# Revit family: 柔性防水套管（A型）
name_source: partatom
category: 管道附件
revit_build: Autodesk Revit 2016 (Build: 20150220_1215(x64)
units: mm (PartAtom-declared; Revit-internal decimal feet)

## family parameters
主体 = 面
共享 = 否
加载时剪切的空心 = 否
圆形连接件大小 = 使用直径
零件类型 = 标准

## types (18) — shared parameters
l5 = 40  [stored 0.131234 ft]
默认高程 = 1219
zero-valued in all types: 高度

## per-type parameters (varying)
| type | D2_2 | D3_2 | D4 | D5 | DN | URL | b | b1 | d2 | d3 | l | l0 | l1 | l2 | n | r | δ2 | δ3 | 螺丝半径 | 角度 | 说明 |
| DN50 | 95 | 65  [stored 0.213255 ft] | 145 | 200 | 50 | www.goujianwu.com | 14  [stored 0.0459318 ft] | 12  [stored 0.0393701 ft] | 91 | 73  [stored 0.239501 ft] | 65  [stored 0.213255 ft] | 28  [stored 0.0918635 ft] | 72 | 30  [stored 0.0984252 ft] | 4 | 73  [stored 0.239501 ft] | 4  [stored 0.0131234 ft] | 8  [stored 0.0262467 ft] | 6  [stored 0.019685 ft] | 90.00° | 找构件就上构件坞 |
| DN65 | 114 | 80 | 165 | 220 | 65  [stored 0.213255 ft] | www.goujianwu.com | 14  [stored 0.0459318 ft] | 12  [stored 0.0393701 ft] | 110  [stored 0.360892 ft] | 88 | 65  [stored 0.213255 ft] | 28  [stored 0.0918635 ft] | 72 | 30  [stored 0.0984252 ft] | 4 | 83 | 4  [stored 0.0131234 ft] | 8  [stored 0.0262467 ft] | 6  [stored 0.019685 ft] | 90.00° | 找构件就上构件坞 |
| DN80 | 127 | 95 | 180 | 235 | 80 | www.goujianwu.com | 18  [stored 0.0590551 ft] | 12  [stored 0.0393701 ft] | 123 | 105 | 65  [stored 0.213255 ft] | 28  [stored 0.0918635 ft] | 76 | 38 | 4 | 90  [stored 0.295276 ft] | 4  [stored 0.0131234 ft] | 10  [stored 0.0328084 ft] | 8  [stored 0.0262467 ft] | 90.00° | 找构件就上构件坞 |
| DN100 | 146 | 114 | 200 | 255 | 100  [stored 0.328084 ft] | www.goujianwu.com | 18  [stored 0.0590551 ft] | 12  [stored 0.0393701 ft] | 142 | 124 | 65  [stored 0.213255 ft] | 28  [stored 0.0918635 ft] | 76 | 38 | 4 | 100  [stored 0.328084 ft] | 5  [stored 0.0164042 ft] | 10  [stored 0.0328084 ft] | 8  [stored 0.0262467 ft] | 90.00° | 找构件就上构件坞 |
| DN125 | 180 | 140 | 235 | 290 | 125 | www.goujianwu.com | 18  [stored 0.0590551 ft] | 12  [stored 0.0393701 ft] | 174 | 150 | 65  [stored 0.213255 ft] | 28  [stored 0.0918635 ft] | 76 | 38 | 6 | 118 | 6  [stored 0.019685 ft] | 10  [stored 0.0328084 ft] | 8  [stored 0.0262467 ft] | 60.00° | 找构件就上构件坞 |
| DN150 | 203 | 165 | 260 | 315 | 150 | www.goujianwu.com | 18  [stored 0.0590551 ft] | 12  [stored 0.0393701 ft] | 197 | 175 | 65  [stored 0.213255 ft] | 28  [stored 0.0918635 ft] | 76 | 38 | 6 | 130 | 6  [stored 0.019685 ft] | 10  [stored 0.0328084 ft] | 8  [stored 0.0262467 ft] | 60.00° | 找构件就上构件坞 |
| DN200 | 265 | 226 | 320 | 375 | 200 | www.goujianwu.com | 18  [stored 0.0590551 ft] | 12  [stored 0.0393701 ft] | 259 | 236 | 65  [stored 0.213255 ft] | 28  [stored 0.0918635 ft] | 76 | 38 | 6 | 160 | 6  [stored 0.019685 ft] | 10  [stored 0.0328084 ft] | 8  [stored 0.0262467 ft] | 60.00° | 找构件就上构件坞 |
| DN250 | 325 | 280 | 380 | 435 | 250 | www.goujianwu.com | 18  [stored 0.0590551 ft] | 12  [stored 0.0393701 ft] | 319 | 290 | 65  [stored 0.213255 ft] | 28  [stored 0.0918635 ft] | 76 | 38 | 8 | 190 | 6  [stored 0.019685 ft] | 10  [stored 0.0328084 ft] | 8  [stored 0.0262467 ft] | 45.00° | 找构件就上构件坞 |
| DN300 | 377 | 333 | 435 | 495 | 300 | www.goujianwu.com | 22  [stored 0.0721785 ft] | 16  [stored 0.0524934 ft] | 369 | 343 | 72 | 32 | 90  [stored 0.295276 ft] | 46 | 8 | 218 | 8  [stored 0.0262467 ft] | 10  [stored 0.0328084 ft] | 10  [stored 0.0328084 ft] | 45.00° | 找构件就上构件坞 |
| DN350 | 426 | 385 | 485 | 545 | 350 | www.goujianwu.com | 22  [stored 0.0721785 ft] | 16  [stored 0.0524934 ft] | 416 | 395 | 72 | 32 | 90  [stored 0.295276 ft] | 46 | 8 | 243 | 10  [stored 0.0328084 ft] | 10  [stored 0.0328084 ft] | 10  [stored 0.0328084 ft] | 45.00° | 找构件就上构件坞 |
| DN400 | 480 | 435 | 540 | 600 | 400 | www.goujianwu.com | 22  [stored 0.0721785 ft] | 16  [stored 0.0524934 ft] | 470 | 445 | 72 | 32 | 90  [stored 0.295276 ft] | 46 | 12 | 270 | 10  [stored 0.0328084 ft] | 10  [stored 0.0328084 ft] | 10  [stored 0.0328084 ft] | 30.00° | 找构件就上构件坞 |
| DN450 | 530 | 488 | 590 | 650 | 450 | www.goujianwu.com | 22  [stored 0.0721785 ft] | 16  [stored 0.0524934 ft] | 520 | 498 | 72 | 32 | 90  [stored 0.295276 ft] | 46 | 12 | 295 | 10  [stored 0.0328084 ft] | 10  [stored 0.0328084 ft] | 10  [stored 0.0328084 ft] | 30.00° | 找构件就上构件坞 |
| DN500 | 585 | 538 | 645 | 705 | 500 | www.goujianwu.com | 22  [stored 0.0721785 ft] | 16  [stored 0.0524934 ft] | 575 | 548 | 72 | 32 | 90  [stored 0.295276 ft] | 46 | 20 | 323 | 10  [stored 0.0328084 ft] | 10  [stored 0.0328084 ft] | 10  [stored 0.0328084 ft] | 18.00° | 找构件就上构件坞 |
| DN600 | 690 | 640 | 755 | 820 | 600 | www.goujianwu.com | 26 | 20  [stored 0.0656168 ft] | 680 | 652 | 75  [stored 0.246063 ft] | 40  [stored 0.131234 ft] | 104 | 54  [stored 0.177165 ft] | 20 | 378 | 10  [stored 0.0328084 ft] | 12  [stored 0.0393701 ft] | 12  [stored 0.0393701 ft] | 18.00° | 找构件就上构件坞 |
| DN700 | 780 | 730 | 845 | 910 | 700 |  | 26 | 20  [stored 0.0656168 ft] | 770 | 742 | 75  [stored 0.246063 ft] | 40  [stored 0.131234 ft] | 104 | 54  [stored 0.177165 ft] | 20 | 423 | 10  [stored 0.0328084 ft] | 12  [stored 0.0393701 ft] | 12  [stored 0.0393701 ft] | 18.00° |  |
| DN800 | 880 | 830 | 950 | 1020 | 800 | www.goujianwu.com | 30  [stored 0.0984252 ft] | 20  [stored 0.0656168 ft] | 870 | 842 | 80 | 40  [stored 0.131234 ft] | 117 | 60 | 20 | 475 | 10  [stored 0.0328084 ft] | 12  [stored 0.0393701 ft] | 27  [stored 0.0885827 ft] | 18.00° | 找构件就上构件坞 |
| DN900 | 980 | 930 | 1050 | 1120 | 900 | www.goujianwu.com | 30  [stored 0.0984252 ft] | 20  [stored 0.0656168 ft] | 970 | 942 | 80 | 40  [stored 0.131234 ft] | 117 | 60 | 20 | 525 | 10  [stored 0.0328084 ft] | 12  [stored 0.0393701 ft] | 27  [stored 0.0885827 ft] | 18.00° | 找构件就上构件坞 |
| DN1000 | 1080 | 1030 | 1150 | 1220 | 1000 | www.goujianwu.com | 30  [stored 0.0984252 ft] | 20  [stored 0.0656168 ft] | 1070 | 1042 | 80 | 40  [stored 0.131234 ft] | 117 | 60 | 24 | 575 | 10  [stored 0.0328084 ft] | 12  [stored 0.0393701 ft] | 27  [stored 0.0885827 ft] | 15.00° | 找构件就上构件坞 |

note: [stored X ft] marks values corroborated as IEEE doubles in the binary element streams (Revit-internal decimal feet)

## geometry (parser evidence)
native form markers: Blend x2
no freeform markers — native parametric forms only
